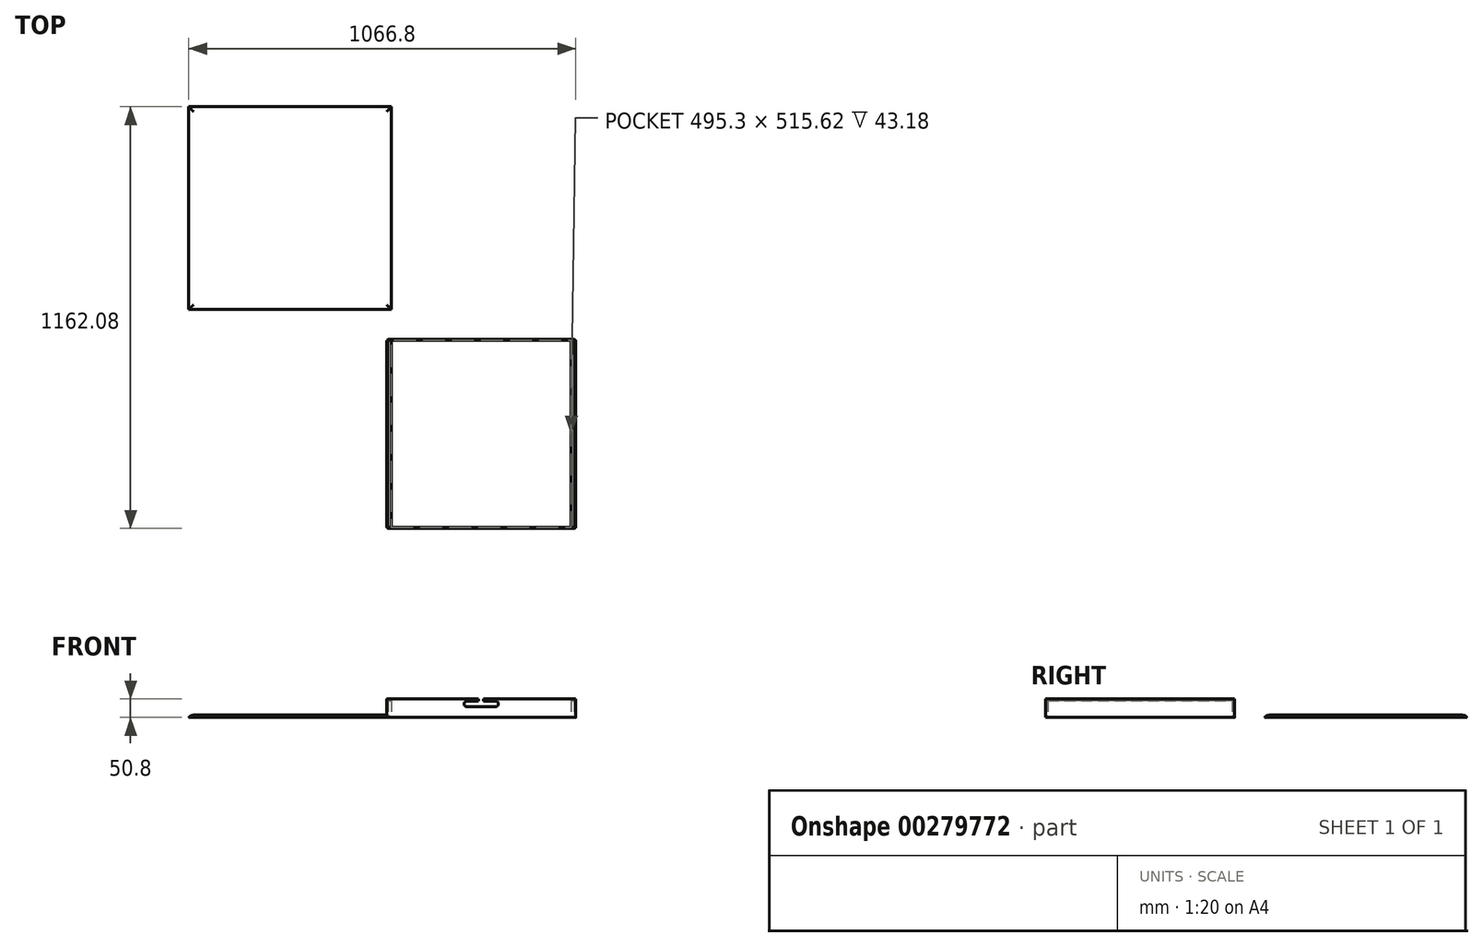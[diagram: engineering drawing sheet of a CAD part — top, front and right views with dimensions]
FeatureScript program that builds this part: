
annotation { "Feature Type Name" : "Feature", "Feature Type Description" : "" }
export const myFeature = defineFeature(function(context is Context, id is Id, definition is map)
    precondition{}
    {
        {
            var Q0;
            Q0=qCreatedBy(makeId("Top.planeOp"),FACE);
            var sketch = newSketch(context, id + "F0", { "sketchPlane" : qUnion([Q0])});
            skLineSegment(sketch, "E0.bottom", {"start": v(69.03, 397.57) * mm, "end": v(589.73, 397.57) * mm});
            skLineSegment(sketch, "E0.top", {"start": v(69.03, -123.13) * mm, "end": v(589.73, -123.13) * mm});
            skLineSegment(sketch, "E0.left", {"start": v(69.03, 397.57) * mm, "end": v(69.03, -123.13) * mm});
            skLineSegment(sketch, "E0.right", {"start": v(589.73, 397.57) * mm, "end": v(589.73, -123.13) * mm});
            skLineSegment(sketch, "E1", {"start": v(69.03, 137.22) * mm, "end": v(589.73, 137.22) * mm, "construction": true});
            skLineSegment(sketch, "E2", {"start": v(589.73, 137.22) * mm, "end": v(329.38, 137.22) * mm, "construction": true});
            skLineSegment(sketch, "E3", {"start": v(329.38, 137.22) * mm, "end": v(329.38, 397.57) * mm, "construction": true});
            skLineSegment(sketch, "E4", {"start": v(329.38, 397.57) * mm, "end": v(329.38, -123.13) * mm, "construction": true});
            skSolve(sketch);
        }
        {
            var Q0;
            Q0=makeQuery(id+"F0.imprint","IMPRINT",FACE,{"disambiguationData":[TD([[makeQuery(id+"F0.imprint","IMPRINT",EDGE,{"derivedFrom":sQuery(id+"F0.wireOp",EDGE,"E0.bottom")}),-1.0]])]});
            var sketch = newSketch(context, id + "F1", { "sketchPlane" : qUnion([Q0])});
            skLineSegment(sketch, "E5.left", {"start": v(81.73, 397.57) * mm, "end": v(81.73, -123.13) * mm});
            skLineSegment(sketch, "E5.right", {"start": v(577.03, 397.57) * mm, "end": v(577.03, -123.13) * mm});
            skLineSegment(sketch, "E6", {"start": v(81.73, 397.57) * mm, "end": v(77.92, 397.57) * mm});
            skLineSegment(sketch, "E7", {"start": v(71.57, 391.22) * mm, "end": v(71.57, -116.6) * mm});
            skLineSegment(sketch, "E8", {"start": v(77.62, -122.94) * mm, "end": v(81.73, -123.13) * mm});
            skLineSegment(sketch, "E9", {"start": v(577.03, -123.13) * mm, "end": v(580.84, -123.13) * mm});
            skLineSegment(sketch, "E10", {"start": v(587.19, -116.78) * mm, "end": v(587.19, 391.22) * mm});
            skLineSegment(sketch, "E11", {"start": v(580.84, 397.57) * mm, "end": v(577.03, 397.57) * mm});
            skPoint(sketch, "E12.visualSharp", {"position": v(587.19, -123.13) * mm});
            skArc(sketch, "E12.filletArc", {"start": v(580.84, -123.13) * mm, "mid": v(585.33, -121.27) * mm, "end": v(587.19, -116.78) * mm});
            skPoint(sketch, "E13.visualSharp", {"position": v(71.57, -122.66) * mm});
            skArc(sketch, "E13.filletArc", {"start": v(71.57, -116.6) * mm, "mid": v(73.32, -120.98) * mm, "end": v(77.62, -122.94) * mm});
            skPoint(sketch, "E14.visualSharp", {"position": v(71.57, 397.57) * mm});
            skArc(sketch, "E14.filletArc", {"start": v(77.92, 397.57) * mm, "mid": v(73.43, 395.71) * mm, "end": v(71.57, 391.22) * mm});
            skPoint(sketch, "E15.visualSharp", {"position": v(587.19, 397.57) * mm});
            skArc(sketch, "E15.filletArc", {"start": v(587.19, 391.22) * mm, "mid": v(585.33, 395.71) * mm, "end": v(580.84, 397.57) * mm});
            skSolve(sketch);
        }
        {
            var Q0;
            Q0=makeQuery(id+"F0.imprint","IMPRINT",FACE,{"disambiguationData":[TD([[makeQuery(id+"F0.imprint","IMPRINT",EDGE,{"derivedFrom":sQuery(id+"F0.wireOp",EDGE,"E0.bottom")}),-1.0]])]});
            extrude(context, id + "F2", {"entities" : qUnion([Q0]), "depth" : 50.8 * mm});
        }
        {
            var Q0;
            Q0=makeQuery(id+"F2.opExtrude","CAP_FACE",FACE,{"disambiguationData":[OSD([sQuery(id+"F0.wireOp",EDGE,"E0.bottom"),sQuery(id+"F0.wireOp",EDGE,"E0.top"),sQuery(id+"F0.wireOp",EDGE,"E0.left"),sQuery(id+"F0.wireOp",EDGE,"E0.right")])],"isStart":false});
            shell(context, id + "F3", {"entities" : qUnion([Q0]), "thickness" : 2.54 * mm});
        }
        {
            var Q0;
            Q0=makeQuery(id+"F0.imprint","IMPRINT",FACE,{"disambiguationData":[TD([[makeQuery(id+"F0.imprint","IMPRINT",EDGE,{"derivedFrom":sQuery(id+"F0.wireOp",EDGE,"E0.bottom")}),-1.0]])]});
            var sketch = newSketch(context, id + "F4", { "sketchPlane" : qUnion([Q0])});
            skLineSegment(sketch, "E16.bottom", {"start": v(56.33, 1013.55) * mm, "end": v(-451.67, 1013.55) * mm});
            skLineSegment(sketch, "E16.top", {"start": v(56.33, 505.55) * mm, "end": v(-451.67, 505.55) * mm});
            skLineSegment(sketch, "E16.left", {"start": v(56.33, 1013.55) * mm, "end": v(56.33, 505.55) * mm});
            skLineSegment(sketch, "E16.right", {"start": v(-451.67, 1013.55) * mm, "end": v(-451.67, 505.55) * mm});
            skLineSegment(sketch, "E17.bottom", {"start": v(-477.07, 480.15) * mm, "end": v(81.73, 480.15) * mm});
            skLineSegment(sketch, "E17.top", {"start": v(-477.07, 1038.95) * mm, "end": v(81.73, 1038.95) * mm});
            skLineSegment(sketch, "E17.left", {"start": v(-477.07, 480.15) * mm, "end": v(-477.07, 1038.95) * mm});
            skLineSegment(sketch, "E17.right", {"start": v(81.73, 480.15) * mm, "end": v(81.73, 1038.95) * mm});
            skSolve(sketch);
        }
        {
            var Q0;
            Q0=makeQuery(id+"F2.opExtrude","SWEPT_EDGE",EDGE,{"disambiguationData":[OSD([sQuery(id+"F0.wireOp",EDGE,"E0.top"),sQuery(id+"F0.wireOp",EDGE,"E0.left")])]});
            var Q1;
            Q1=makeQuery(id+"F2.opExtrude","SWEPT_EDGE",EDGE,{"disambiguationData":[OSD([sQuery(id+"F0.wireOp",EDGE,"E0.top"),sQuery(id+"F0.wireOp",EDGE,"E0.right")])]});
            var Q2;
            Q2=makeQuery(id+"F2.opExtrude","SWEPT_EDGE",EDGE,{"disambiguationData":[OSD([sQuery(id+"F0.wireOp",EDGE,"E0.bottom"),sQuery(id+"F0.wireOp",EDGE,"E0.right")])]});
            var Q3;
            Q3=makeQuery(id+"F2.opExtrude","SWEPT_EDGE",EDGE,{"disambiguationData":[OSD([sQuery(id+"F0.wireOp",EDGE,"E0.bottom"),sQuery(id+"F0.wireOp",EDGE,"E0.left")])]});
            fillet(context, id + "F5", {"entities" : qUnion([Q0, Q1, Q2, Q3]), "radius" : 5.08 * mm, "tangentPropagation" : true, "allowEdgeOverflow" : false});
        }
        {
            var Q0;
            Q0=makeQuery(id+"F4.imprint","IMPRINT",FACE,{"disambiguationData":[TD([[makeQuery(id+"F4.imprint","IMPRINT",EDGE,{"derivedFrom":sQuery(id+"F4.wireOp",EDGE,"E16.bottom")}),1.0]])]});
            extrude(context, id + "F6", {"entities" : qUnion([Q0]), "depth" : 6.35 * mm});
        }
        {
            var Q0;
            Q0=makeQuery(id+"F4.imprint","IMPRINT",FACE,{"disambiguationData":[TD([[makeQuery(id+"F4.imprint","IMPRINT",EDGE,{"derivedFrom":sQuery(id+"F4.wireOp",EDGE,"E16.bottom")}),-1.0]])]});
            extrude(context, id + "F7", {"entities" : qUnion([Q0]), "operationType" : NewBodyOperationType.ADD, "depth" : 6.35 * mm});
        }
        {
            var Q0;
            {var subQ0=sQuery(id+"F4.wireOp",EDGE,"jfDjBv7M-59MB-g6S8-UM37-as3fPkQULSKO");var subQ1=sQuery(id+"F4.wireOp",EDGE,"E16.left");var subQ2=sQuery(id+"F4.wireOp",EDGE,"E16.top");var subQ3=sQuery(id+"F4.wireOp",EDGE,"E16.bottom");Q0=makeQuery(id+"F7.boolean.opBoolean","MERGE",FACE,{"derivedFrom":[makeQuery(id+"F6.opExtrude","CAP_FACE",FACE,{"disambiguationData":[OSD([subQ3,subQ2,subQ1,subQ0])],"isStart":false}),makeQuery(id+"F7.opExtrude","CAP_FACE",FACE,{"disambiguationData":[OSD([subQ3,subQ2,subQ1,subQ0,sQuery(id+"F4.wireOp",EDGE,"E17.bottom"),sQuery(id+"F4.wireOp",EDGE,"E17.top"),sQuery(id+"F4.wireOp",EDGE,"E17.left"),sQuery(id+"F4.wireOp",EDGE,"E17.right")])],"isStart":false})]});}
            fillet(context, id + "F8", {"entities" : qUnion([Q0]), "radius" : 16.5 * mm, "tangentPropagation" : true, "allowEdgeOverflow" : false});
        }
        {
            var Q0;
            Q0=makeQuery(id+"F2.opExtrude","SWEPT_FACE",FACE,{"disambiguationData":[OSD([sQuery(id+"F0.wireOp",EDGE,"E0.top")])]});
            var sketch = newSketch(context, id + "F9", { "sketchPlane" : qUnion([Q0])});
            skLineSegment(sketch, "E18.bottom", {"start": v(369.93, 30.27) * mm, "end": v(288.82, 30.27) * mm});
            skLineSegment(sketch, "E18.top", {"start": v(369.93, 44.8) * mm, "end": v(288.82, 44.8) * mm});
            skLineSegment(sketch, "E18.left", {"start": v(376.28, 36.62) * mm, "end": v(376.28, 38.46) * mm});
            skLineSegment(sketch, "E18.right", {"start": v(282.47, 36.62) * mm, "end": v(282.47, 38.46) * mm});
            skPoint(sketch, "E18.middle", {"position": v(329.38, 37.54) * mm});
            skPoint(sketch, "E18.middle.positionSnap0", {"position": v(329.38, 0) * mm});
            skPoint(sketch, "E18.centerSnap0", {"position": v(329.38, 0) * mm});
            skPoint(sketch, "E19.visualSharp", {"position": v(282.47, 44.8) * mm});
            skArc(sketch, "E19.filletArc", {"start": v(288.82, 44.8) * mm, "mid": v(284.33, 42.95) * mm, "end": v(282.47, 38.46) * mm});
            skPoint(sketch, "E20.visualSharp", {"position": v(282.47, 30.27) * mm});
            skArc(sketch, "E20.filletArc", {"start": v(282.47, 36.62) * mm, "mid": v(284.33, 32.13) * mm, "end": v(288.82, 30.27) * mm});
            skPoint(sketch, "E21.visualSharp", {"position": v(376.28, 44.8) * mm});
            skArc(sketch, "E21.filletArc", {"start": v(376.28, 38.46) * mm, "mid": v(374.42, 42.95) * mm, "end": v(369.93, 44.8) * mm});
            skPoint(sketch, "E22.visualSharp", {"position": v(376.28, 30.27) * mm});
            skArc(sketch, "E22.filletArc", {"start": v(369.93, 30.27) * mm, "mid": v(374.42, 32.13) * mm, "end": v(376.28, 36.62) * mm});
            skSolve(sketch);
        }
        {
            var Q0;
            Q0 = qSketchRegion(id + "F9", true);
            extrude(context, id + "F10", {"entities" : qUnion([Q0]), "operationType" : NewBodyOperationType.REMOVE, "endBound" : BoundingType.THROUGH_ALL, "oppositeDirection" : true, "depth" : 25.4 * mm});
        }
        {
            var Q0;
            Q0 = qSketchRegion(id + "F1", true);
            extrude(context, id + "F11", {"entities" : qUnion([Q0]), "operationType" : NewBodyOperationType.ADD, "depth" : 45.72 * mm});
        }
        {
            var Q0;
            Q0=makeQuery(id+"F9.imprint","IMPRINT",FACE,{"disambiguationData":[TD([[makeQuery(id+"F9.imprint","IMPRINT",EDGE,{"derivedFrom":sQuery(id+"F9.wireOp",EDGE,"E18.bottom")}),1.0]])]});
            var sketch = newSketch(context, id + "F12", { "sketchPlane" : qUnion([Q0])});
            skLineSegment(sketch, "E23", {"start": v(321.77, 37.16) * mm, "end": v(321.77, 50.99) * mm});
            skLineSegment(sketch, "E24", {"start": v(321.77, 50.99) * mm, "end": v(335.5, 50.99) * mm});
            skLineSegment(sketch, "E25", {"start": v(335.5, 50.99) * mm, "end": v(335.5, 42.08) * mm});
            skLineSegment(sketch, "E26", {"start": v(335.5, 42.08) * mm, "end": v(321.77, 37.16) * mm});
            skSolve(sketch);
        }
        {
            var Q0;
            Q0 = qSketchRegion(id + "F12", true);
            extrude(context, id + "F13", {"entities" : qUnion([Q0]), "operationType" : NewBodyOperationType.REMOVE, "endBound" : BoundingType.THROUGH_ALL, "oppositeDirection" : true, "depth" : 25.4 * mm});
        }
    });
